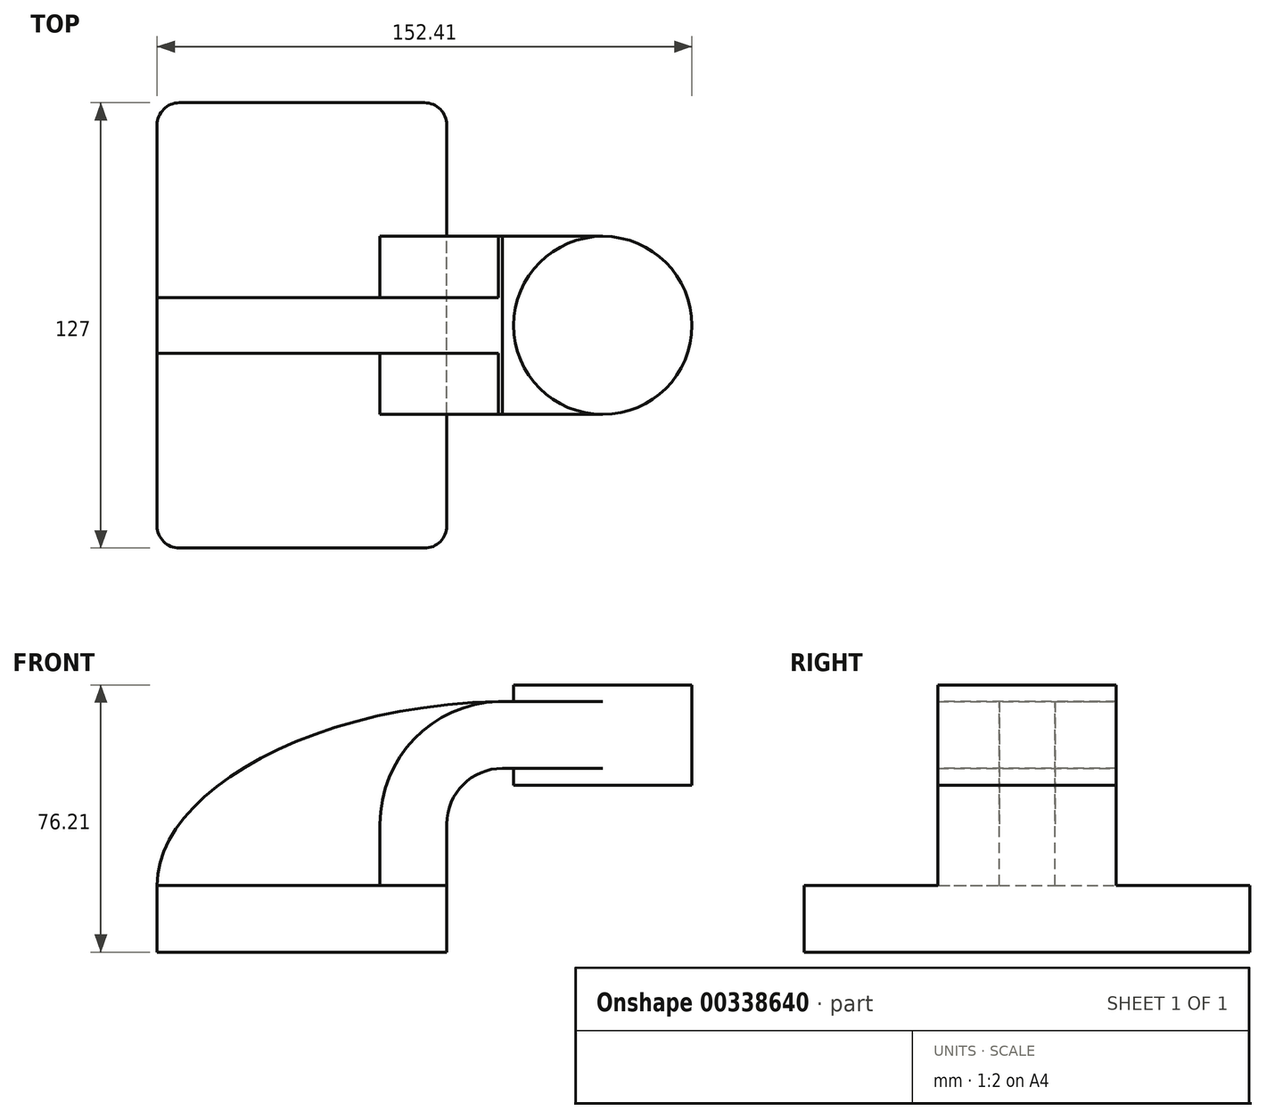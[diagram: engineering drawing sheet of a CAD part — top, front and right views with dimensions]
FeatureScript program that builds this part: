
annotation { "Feature Type Name" : "Feature", "Feature Type Description" : "" }
export const myFeature = defineFeature(function(context is Context, id is Id, definition is map)
    precondition{}
    {
        {
            var Q0;
            Q0=qCreatedBy(makeId("Front.planeOp"),FACE);
            var sketch = newSketch(context, id + "F0", { "sketchPlane" : qUnion([Q0])});
            skLineSegment(sketch, "E0.bottom", {"start": v(-41.28, 9.52) * mm, "end": v(41.27, 9.53) * mm});
            skLineSegment(sketch, "E0.top", {"start": v(-41.28, -9.53) * mm, "end": v(41.28, -9.53) * mm});
            skLineSegment(sketch, "E0.left", {"start": v(-41.28, 9.52) * mm, "end": v(-41.28, -9.53) * mm});
            skLineSegment(sketch, "E0.right", {"start": v(41.27, 9.53) * mm, "end": v(41.28, -9.52) * mm});
            skPoint(sketch, "E0.middle", {"position": v(0, 0) * mm});
            skLineSegment(sketch, "E1.bottom", {"start": v(60.33, 66.68) * mm, "end": v(111.12, 66.68) * mm});
            skLineSegment(sketch, "E1.top", {"start": v(60.33, 38.1) * mm, "end": v(111.12, 38.1) * mm});
            skLineSegment(sketch, "E1.left", {"start": v(60.33, 66.68) * mm, "end": v(60.33, 38.1) * mm});
            skLineSegment(sketch, "E1.right", {"start": v(111.12, 66.68) * mm, "end": v(111.12, 38.1) * mm});
            skPoint(sketch, "E1.middle", {"position": v(85.72, 52.39) * mm});
            skLineSegment(sketch, "E2", {"start": v(41.27, 9.53) * mm, "end": v(41.27, 27) * mm});
            skArc(sketch, "E3", {"start": v(41.27, 27) * mm, "mid": v(45.92, 38.23) * mm, "end": v(57.15, 42.88) * mm});
            skLineSegment(sketch, "E4", {"start": v(57.15, 42.88) * mm, "end": v(85.72, 42.88) * mm});
            skLineSegment(sketch, "E5.0", {"start": v(57.15, 61.93) * mm, "end": v(85.72, 61.93) * mm});
            skArc(sketch, "E5.1", {"start": v(22.22, 27) * mm, "mid": v(32.45, 51.7) * mm, "end": v(57.15, 61.93) * mm});
            skLineSegment(sketch, "E5.2", {"start": v(22.22, 9.53) * mm, "end": v(22.22, 27) * mm});
            skFitSpline(sketch, "E6", {"points": [v(-41.28, 9.52) * mm, v(57.15, 61.93) * mm], "startDerivative": vector(-1.6, 74.2) * mm, "endDerivative": vector(171.45, 2.47) * mm});
            skLineSegment(sketch, "E7", {"start": v(85.72, 66.68) * mm, "end": v(85.72, 38.1) * mm});
            skSolve(sketch);
        }
        {
            var Q0;
            Q0=makeQuery(id+"F0.imprint","IMPRINT",FACE,{"disambiguationData":[TD([[makeQuery(id+"F0.imprint","IMPRINT",EDGE,{"derivedFrom":sQuery(id+"F0.wireOp",EDGE,"E0.top")}),1.0]])]});
            extrude(context, id + "F1", {"entities" : qUnion([Q0]), "depth" : 127 * mm, "symmetric" : true});
        }
        {
            var Q0;
            {var subQ6=sQuery(id+"F0.wireOp",EDGE,"E2");Q0=makeQuery(id+"F0.imprint","IMPRINT",FACE,{"disambiguationData":[TD([[makeQuery(id+"F0.imprint","IMPRINT",EDGE,{"derivedFrom":subQ6}),1.0]])]});}
            var Q1;
            {var subQ0=sQuery(id+"F0.wireOp",EDGE,"E5.0");var subQ1=sQuery(id+"F0.wireOp",EDGE,"E1.left");var subQ2=makeQuery(id+"F0.imprint","INTERSECT",VERTEX,{"derivedFrom":[subQ1,subQ0]});Q1=makeQuery(id+"F0.imprint","IMPRINT",FACE,{"disambiguationData":[TD([[makeQuery(id+"F0.imprint","IMPRINT",EDGE,{"disambiguationData":[TD([[subQ2,-1.0]])],"derivedFrom":subQ1}),1.0]])]});}
            extrude(context, id + "F2", {"entities" : qUnion([Q0, Q1]), "operationType" : NewBodyOperationType.ADD, "depth" : 50.8 * mm, "symmetric" : true});
        }
        {
            var Q0;
            {var subQ3=sQuery(id+"F0.wireOp",EDGE,"E5.2");Q0=makeQuery(id+"F0.imprint","IMPRINT",FACE,{"disambiguationData":[TD([[makeQuery(id+"F0.imprint","IMPRINT",EDGE,{"derivedFrom":subQ3}),1.0]])]});}
            extrude(context, id + "F3", {"entities" : qUnion([Q0]), "operationType" : NewBodyOperationType.ADD, "depth" : 15.88 * mm, "symmetric" : true});
        }
        {
            var Q0;
            {var subQ4=sQuery(id+"F0.wireOp",EDGE,"E1.right");Q0=makeQuery(id+"F0.imprint","IMPRINT",FACE,{"disambiguationData":[TD([[makeQuery(id+"F0.imprint","IMPRINT",EDGE,{"derivedFrom":subQ4}),-1.0]])]});}
            var Q1;
            Q1=sQuery(id+"F0.wireOp",EDGE,"E7");
            revolve(context, id + "F4", {"operationType" : NewBodyOperationType.ADD, "entities" : qUnion([Q0]), "axis" : qUnion([Q1]), "revolveType" : RevolveType.FULL});
        }
        {
            var Q0;
            Q0=makeQuery(id+"F1.opExtrude","CAP_EDGE",EDGE,{"disambiguationData":[OSD([sQuery(id+"F0.wireOp",EDGE,"E0.left")])],"isStart":false});
            var Q1;
            Q1=makeQuery(id+"F1.opExtrude","CAP_EDGE",EDGE,{"disambiguationData":[OSD([sQuery(id+"F0.wireOp",EDGE,"E0.right")])],"isStart":false});
            var Q2;
            Q2=makeQuery(id+"F1.opExtrude","CAP_EDGE",EDGE,{"disambiguationData":[OSD([sQuery(id+"F0.wireOp",EDGE,"E0.right")])],"isStart":true});
            var Q3;
            Q3=makeQuery(id+"F1.opExtrude","CAP_EDGE",EDGE,{"disambiguationData":[OSD([sQuery(id+"F0.wireOp",EDGE,"E0.left")])],"isStart":true});
            fillet(context, id + "F5", {"entities" : qUnion([Q0, Q1, Q2, Q3]), "radius" : 6.35 * mm, "tangentPropagation" : true, "allowEdgeOverflow" : false});
        }
    });
